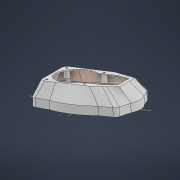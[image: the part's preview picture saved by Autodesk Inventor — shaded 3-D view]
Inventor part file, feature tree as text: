
AUTODESK INVENTOR PART (.ipt)
format: ipt  version: 2021 (Build 250183000, 183)  size: 1,366,528 bytes
history: native  units: mm
features: sketch x5, other x4, extrude x3, plane x2, surface_op x2, thicken_offset x1, loft x1
ambient origin geometry x8: Origin, YZ Plane, XZ Plane, XY Plane, X Axis, Y Axis, Z Axis, Center Point
bodies: Solid1 (feature_tree)
feature tree (18):
  plane  "Work Plane1"
  sketch  "Sketch2"  dims[d2=5.8mm d4=45.0deg]
  sketch  "Sketch1"  dims[d0=54.0mm d1=127.0mm]
  plane  "Work Plane2"
  sketch  "Sketch4"  dims[d11=83.5mm d12=59.5mm]
  sketch  "Sketch3"  dims[d6=40.0mm d8=360.0deg d10=83.5mm]
  surface_op  "Stitch Surface1"
  thicken_offset  "Thicken1"
  extrude  "Extrusion1"  Depth=127.0mm
  extrude  "Extrusion2"  TaperAngle=45.0deg  [1 undecoded]
  other  "Srf4"
  other  "Srf5"
  other  "Srf6"
  other  "Srf7"
  sketch  "Sketch6"  dims[d13=59.5mm d14=167.0mm d15=119.0mm d16=3.8mm d18=3.8mm d19=3.8mm d20=3.8mm d22=5.0mm d23=10.0mm d24=10.0mm d25=10.0mm d26=10.0mm d27=12.0mm d28=12.0mm d29=12.0mm d30=12.0mm d31=-34.0mm d32=27.925268mm d33=118.0mm d34=82.0mm d35=10.0mm d47=10.0mm d48=10.0mm d49=100.0mm d50=25.0mm d51=25.0mm d52=8.0mm d53=8.0mm d54=0.0mm d55=90.0deg d56=0.0mm d57=90.0deg d58=10.0mm d59=0.0mm d60=2.49mm d61=20.0mm d62=20.0mm d63=0.0mm d64=20.0mm d65=0.0mm]
  loft  "LoftSrf2"
  extrude  "ExtrusionSrf2"  Depth=59.5mm
  surface_op  "Boundary Patch2"
note: 1 required parameter value undecoded (feature->parameter linkage not recoverable at this tier; creation-order binding heuristic only, values carry confidence <= 0.55)
